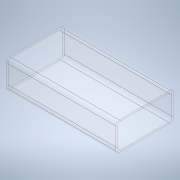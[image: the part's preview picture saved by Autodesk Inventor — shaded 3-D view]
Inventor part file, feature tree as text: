
AUTODESK INVENTOR PART (.ipt)
format: ipt  version: 2022 (Build 260153000, 153)  size: 121,856 bytes
history: native  units: in
note: dims shown in document units (in); Inventor stores cm internally (conversion verified against a paired STEP export)
features: extrude x1, fillet x1, sketch x1
ambient origin geometry x8: Origin, YZ Plane, XZ Plane, XY Plane, X Axis, Y Axis, Z Axis, Center Point
bodies: Solid1 (feature_tree)
feature tree (3):
  extrude  "Extrusion1"  Depth=0.6299in
  fillet  "Fillet1"  Radius=0.0197in
  sketch  "Sketch1"  dims[d0=0.2894in d1=0.6299in d2=0.0197in d3=1.1024in d4=0.0in d5=0.0394in]
